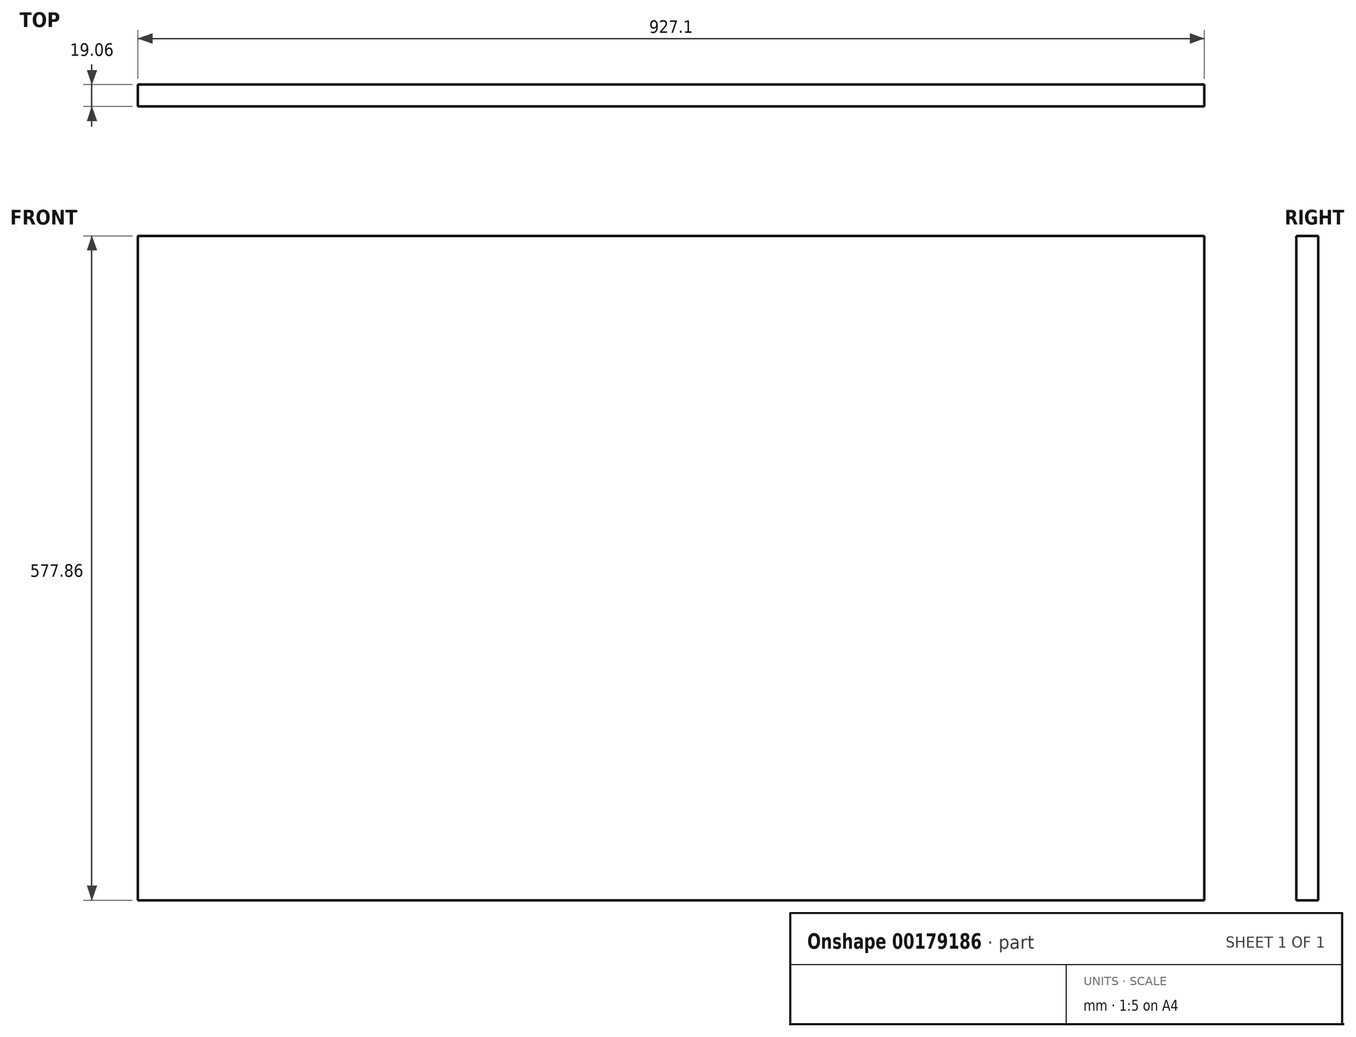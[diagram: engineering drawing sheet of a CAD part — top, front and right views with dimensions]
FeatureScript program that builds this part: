
annotation { "Feature Type Name" : "Feature", "Feature Type Description" : "" }
export const myFeature = defineFeature(function(context is Context, id is Id, definition is map)
    precondition{}
    {
        {
            var Q0;
            Q0=qCreatedBy(makeId("Front.planeOp"),FACE);
            var sketch = newSketch(context, id + "F0", { "sketchPlane" : qUnion([Q0])});
            skLineSegment(sketch, "E0.bottom", {"start": v(-247.9, 288.93) * mm, "end": v(679.2, 288.93) * mm});
            skLineSegment(sketch, "E0.top", {"start": v(-247.9, -288.93) * mm, "end": v(679.2, -288.93) * mm});
            skLineSegment(sketch, "E0.left", {"start": v(-247.9, 288.93) * mm, "end": v(-247.9, -288.93) * mm});
            skLineSegment(sketch, "E0.right", {"start": v(679.2, 288.93) * mm, "end": v(679.2, -288.93) * mm});
            skLineSegment(sketch, "E1", {"start": v(-247.9, 0) * mm, "end": v(679.2, 0) * mm});
            skSolve(sketch);
        }
        {
            var Q0;
            {var subQ0=sQuery(id+"F0.wireOp",EDGE,"E0.bottom");Q0=makeQuery(id+"F0.imprint","IMPRINT",FACE,{"disambiguationData":[TD([[makeQuery(id+"F0.imprint","IMPRINT",EDGE,{"derivedFrom":subQ0}),-1.0]])]});}
            var Q1;
            {var subQ0=sQuery(id+"F0.wireOp",EDGE,"E0.top");Q1=makeQuery(id+"F0.imprint","IMPRINT",FACE,{"disambiguationData":[TD([[makeQuery(id+"F0.imprint","IMPRINT",EDGE,{"derivedFrom":subQ0}),1.0]])]});}
            extrude(context, id + "F1", {"entities" : qUnion([Q0, Q1]), "depth" : 19.05 * mm, "symmetric" : true});
        }
    });
